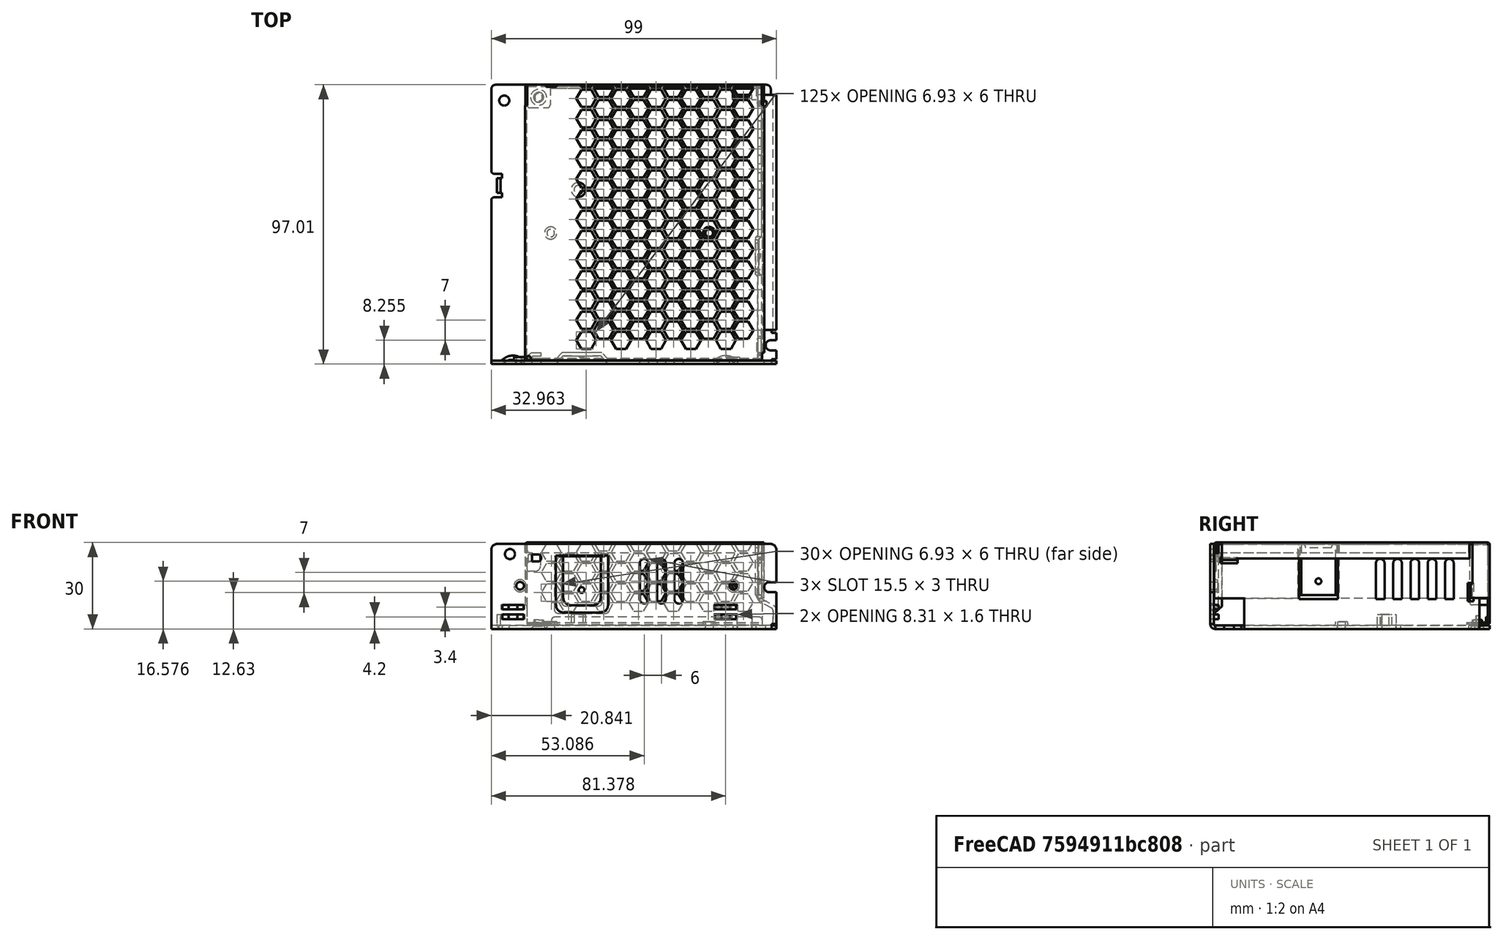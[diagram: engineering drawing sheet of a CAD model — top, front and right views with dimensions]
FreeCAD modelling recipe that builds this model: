
FCSTD DOCUMENT  (FreeCAD 1.0R39319 (Git))
Label: LRS-75
License: All rights reserved
LicenseURL: https://en.wikipedia.org/wiki/All_rights_reserved
objects: Part::Feature×3, PartDesign::CoordinateSystem×3, Part::Refine×3, App::Part×1
note: 9 computed .brp shape members not serialized (recipe doc carries the construction recipe); baked Part::Feature solids carry a one-line shape summary decoded from their .brp

FEATURE [Part::Feature] Part__Feature  label="TY_2"
  Placement = pos=(-30,0,0.2) rot=(0,0,1;0rad)
  shape: bbox 99.02 x 97.65 x 30.2 mm, 1471 faces (baked)
FEATURE [Part::Feature] Part__Feature001  label="TN_1_1_1_1_1"
  Placement = pos=(-299.667,159.449,37.1256) rot=(0,1,0;1.5708rad)
  shape: bbox 18 x 50.7 x 15 mm, 182 faces (baked)
FEATURE [Part::Feature] Part__Feature002  label="PCB"
  shape: bbox 92 x 94.4 x 1.6 mm, 16 faces (baked)
FEATURE [PartDesign::CoordinateSystem] stack_attach
  AttacherType = Attacher::AttachEngine3D
  AttachmentSupport = -> [Part__Feature]
  MapMode = 11
  Placement = pos=(-224.029,248.825,-6.6) rot=(0,0,1;3.14104rad)
FEATURE [PartDesign::CoordinateSystem] screw1
  AttacherType = Attacher::AttachEngine3D
  AttachmentSupport = -> [Part__Feature]
  MapMode = 11
  Placement = pos=(-295.167,294.825,-5.4) rot=(-0.706748,0.707465,0;3.14159rad)
FEATURE [PartDesign::CoordinateSystem] screw2
  AttacherType = Attacher::AttachEngine3D
  AttachmentSupport = -> [Part__Feature]
  MapMode = 11
  Placement = pos=(-202.667,209.825,-5.4) rot=(-0.086033,0.996292,0;3.14159rad)
FEATURE [App::Part] LRS_75_ASM  label="LRS-75_ASM"
  Group = -> [Part__Feature,Part__Feature001,Part__Feature002,stack_attach,screw1,screw2]
  Origin = -> Origin001
FEATURE [Part::Refine] Part__Feature003  label="TY_003"
  Source = -> Part__Feature
FEATURE [Part::Refine] Part__Feature004  label="TN_1_1_1_1_002"
  Source = -> Part__Feature001
FEATURE [Part::Refine] Part__Feature005  label="PCB001"
  Source = -> Part__Feature002
